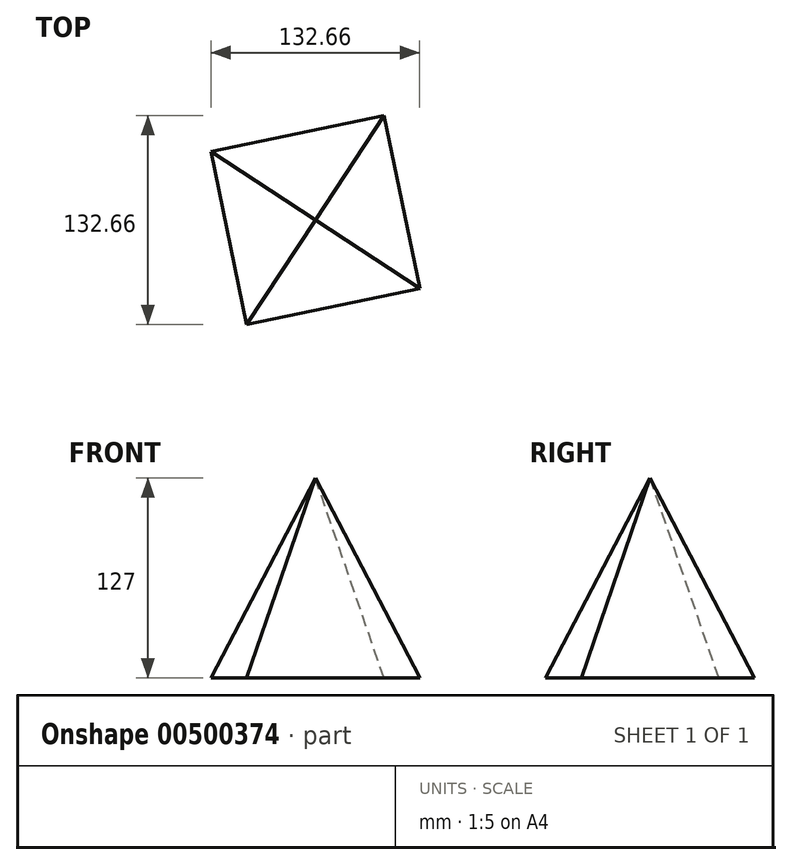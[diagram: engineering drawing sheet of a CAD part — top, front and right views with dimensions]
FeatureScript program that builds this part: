
annotation { "Feature Type Name" : "Feature", "Feature Type Description" : "" }
export const myFeature = defineFeature(function(context is Context, id is Id, definition is map)
    precondition{}
    {
        {
            var Q0;
            Q0=qCreatedBy(makeId("Top.planeOp"),FACE);
            var sketch = newSketch(context, id + "F0", { "sketchPlane" : qUnion([Q0])});
            skCircle(sketch, "E0.cCircle", {"center": v(0, 0) * mm, "radius": 79.35 * mm, "construction": true});
            skLineSegment(sketch, "E0.0", {"start": v(-43.56, -66.33) * mm, "end": v(-66.33, 43.56) * mm});
            skLineSegment(sketch, "E0.1", {"start": v(-66.33, 43.56) * mm, "end": v(43.56, 66.33) * mm});
            skLineSegment(sketch, "E0.2", {"start": v(43.56, 66.33) * mm, "end": v(66.33, -43.56) * mm});
            skLineSegment(sketch, "E0.3", {"start": v(66.33, -43.56) * mm, "end": v(-43.56, -66.33) * mm});
            skSolve(sketch);
        }
        {
            var Q0;
            Q0=qCreatedBy(makeId("Top.planeOp"),FACE);
            cPlane(context, id + "F1", {"entities" : qUnion([Q0]), "cplaneType" : CPlaneType.OFFSET, "offset" : 127 * mm, "width" : 152.4 * mm, "height" : 152.4 * mm});
        }
        {
            var Q0;
            Q0=qCreatedBy(id+"F1.planeOp",FACE);
            var sketch = newSketch(context, id + "F2", { "sketchPlane" : qUnion([Q0])});
            skPoint(sketch, "E1", {"position": v(0, 0) * mm});
            skSolve(sketch);
        }
        {
            var Q0;
            Q0=makeQuery(id+"F0.imprint","IMPRINT",FACE,{"disambiguationData":[TD([[makeQuery(id+"F0.imprint","IMPRINT",EDGE,{"derivedFrom":sQuery(id+"F0.wireOp",EDGE,"E0.0")}),-1.0]])]});
            var Q1;
            Q1=sQuery(id+"F2.wireOp",VERTEX,"E1");
            loft(context, id + "F3", {"sheetProfilesArray" : [{ "sheetProfileEntities" : qUnion([Q0]) }, { "sheetProfileEntities" : qUnion([Q1]) }]});
        }
    });
